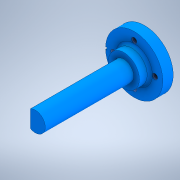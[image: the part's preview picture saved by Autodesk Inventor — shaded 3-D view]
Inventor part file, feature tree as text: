
AUTODESK INVENTOR PART (.ipt)
format: ipt  version: 2021 (Build 250183000, 183)  size: 190,464 bytes
history: native  units: mm
features: sketch x5, extrude x4, other x1, hole x1, plane x1, fillet x1
ambient origin geometry x8: Origin, YZ Plane, XZ Plane, XY Plane, X Axis, Y Axis, Z Axis, Center Point
bodies: Body1 (feature_tree)
feature tree (13):
  other  "Sólido1"
  extrude  "Extrusión1"  Depth=4.0mm
  hole  "Agujero1"  [1 undecoded]
  extrude  "Extrusión2"  Depth=4.0mm TaperAngle=0.0deg
  extrude  "Extrusión3"  Depth=1.0mm
  plane  "Plano de trabajo1"
  extrude  "Extrusión4"  Depth=1.0mm
  fillet  "Empalme5"  Radius=8.0mm
  sketch  "Boceto1"  dims[d1=4.0mm d2=0.0mm d7=2.1mm]
  sketch  "Boceto2"  dims[d8=2.1mm d9=2.1mm]
  sketch  "Boceto3"  dims[d10=2.1mm]
  sketch  "Boceto4"  dims[d11=2.013mm d12=5.0mm d13=2.5mm d14=2.0mm d15=90.0deg d16=8.0mm d17=20.594885mm d19=4.0mm d20=0.0mm]
  sketch  "Boceto7"  dims[d22=34.0mm d23=0.0mm d29=1.9mm d31=8.0mm d32=8.0mm d33=8.0mm d34=1.0mm d35=4.0mm d36=0.5mm d37=0.0mm d38=2.0mm d39=1.0mm]
note: 1 required parameter value undecoded (feature->parameter linkage not recoverable at this tier; creation-order binding heuristic only, values carry confidence <= 0.55)
